# Revit family: P191568KX-104c_KMHP519E
name_source: partatom
category: Specialty Equipment
units: mm (PartAtom-declared; Revit-internal decimal feet)

## family parameters
Always vertical = Yes
Cut with Voids When Loaded = No
Enable Cutting in Views = No
Maintain Annotation Orientation = No
Part Type = Normal
Room Calculation Point = No
Round Connector Dimension = Use Diameter
Shared = No
Work Plane-Based = No

## types (1)
- KMHP519ESS
    Amps = 15 A
    Body Material = ARCAT - Metal - Steel - Black
    Clearance Material = ARCAT - Clearance
    Default Elevation = 0"
    Depth = 17"
    Description = 1200-Watt Convection Microwave with High-Speed Cooking - 30"
    Dimension Guide = http://access.whirlpool.com Guide&sku=KMHP519ESS&language=EN
    Door Material = ARCAT - Metal - Steel - Stainless
    Family Name = COOKING
    Feature 1 = High-Speed Cooking
    Feature 2 = Convection Cooking
    Feature 3 = Professionally-Inspired Design Including Handle, Badge, Graphics, Chrome Chamfer.
Professionally-Inspired Design Including Handle, Badge, Graphics, Chrome Chamfer.
    Glass Material = ARCAT - Glass - Black
    Handle Material = ARCAT - Metal - Steel - Stainless
    Height = 17 1/8"
    Installation-Fabrication = http://access.whirlpool.com Instruction&sku=KMHP519ESS&language=EN
    Manufacturer = KitchenAid
    Model = KMHP519ESS
    Voltage = 0 V
    Width = 30"

## geometry (parser evidence)
native form markers: Sweep x4
no freeform markers — native parametric forms only
